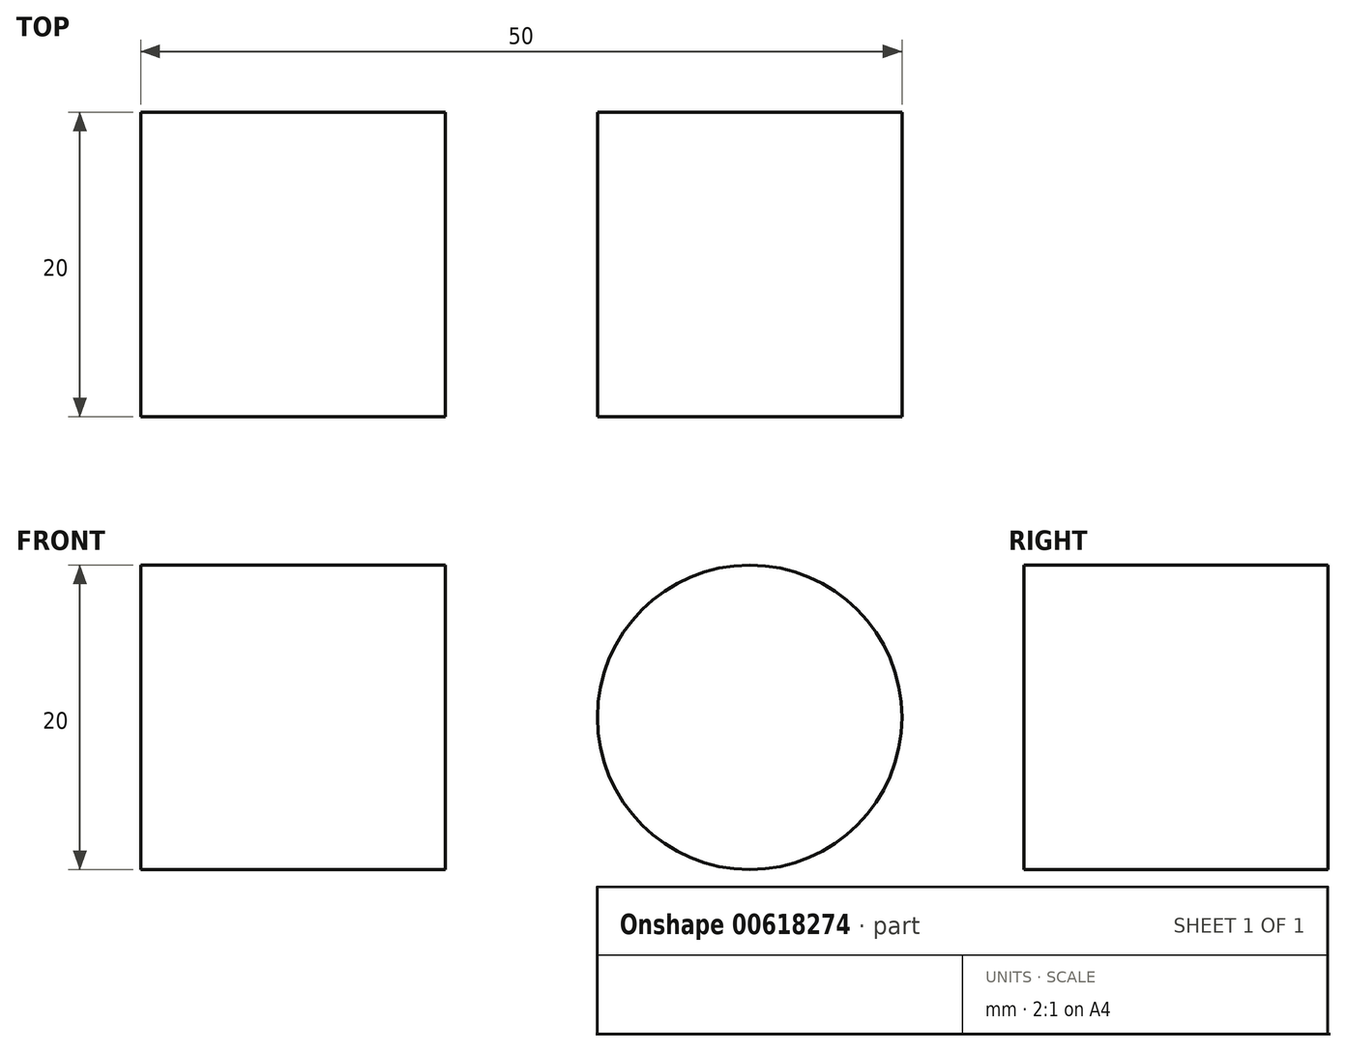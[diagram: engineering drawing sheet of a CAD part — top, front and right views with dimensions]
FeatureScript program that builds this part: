
annotation { "Feature Type Name" : "Feature", "Feature Type Description" : "" }
export const myFeature = defineFeature(function(context is Context, id is Id, definition is map)
    precondition{}
    {
        {
            var Q0;
            Q0=qCreatedBy(makeId("Front.planeOp"),FACE);
            var sketch = newSketch(context, id + "F0", { "sketchPlane" : qUnion([Q0])});
            skLineSegment(sketch, "E0.bottom", {"start": v(10, 10) * mm, "end": v(-10, 10) * mm});
            skLineSegment(sketch, "E0.top", {"start": v(10, -10) * mm, "end": v(-10, -10) * mm});
            skLineSegment(sketch, "E0.left", {"start": v(10, 10) * mm, "end": v(10, -10) * mm});
            skLineSegment(sketch, "E0.right", {"start": v(-10, 10) * mm, "end": v(-10, -10) * mm});
            skPoint(sketch, "E0.middle", {"position": v(0, 0) * mm});
            skCircle(sketch, "E1", {"center": v(30, 0) * mm, "radius": 10 * mm});
            skSolve(sketch);
        }
        {
            var Q0;
            Q0 = qSketchRegion(id + "F0", true);
            extrude(context, id + "F1", {"entities" : qUnion([Q0]), "depth" : 20 * mm, "offsetDistance" : 25.4 * mm});
        }
    });
